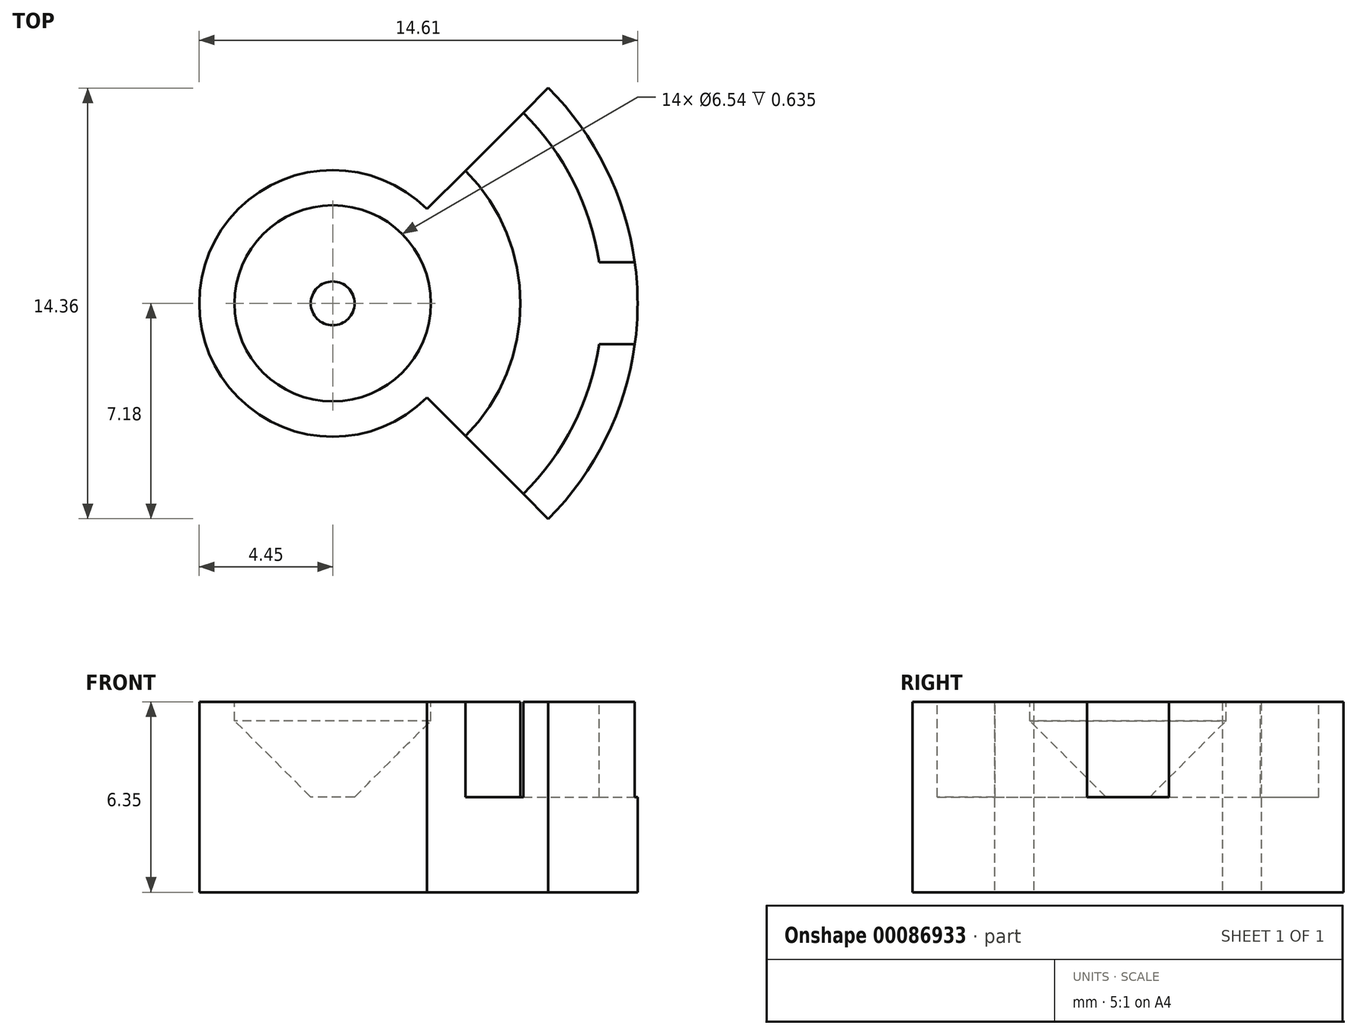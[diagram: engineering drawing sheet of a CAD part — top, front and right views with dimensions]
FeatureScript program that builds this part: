
annotation { "Feature Type Name" : "Feature", "Feature Type Description" : "" }
export const myFeature = defineFeature(function(context is Context, id is Id, definition is map)
    precondition{}
    {
        {
            var Q0;
            Q0=qCreatedBy(makeId("Top.planeOp"),FACE);
            var sketch = newSketch(context, id + "F0", { "sketchPlane" : qUnion([Q0])});
            skCircle(sketch, "E0", {"center": v(0, 0) * mm, "radius": 3.27 * mm});
            skCircle(sketch, "E1", {"center": v(0, 0) * mm, "radius": 4.45 * mm});
            skLineSegment(sketch, "E2", {"start": v(0, 11.64) * mm, "end": v(0, -10.82) * mm, "construction": true});
            skArc(sketch, "E3", {"start": v(-4.45, 0) * mm, "mid": v(-4.1, 1.7) * mm, "end": v(-3.14, 3.14) * mm});
            skLineSegment(sketch, "E4", {"start": v(0, 0) * mm, "end": v(-7.18, 7.18) * mm, "construction": true});
            skArc(sketch, "E5", {"start": v(-10.16, 0) * mm, "mid": v(-9.39, 3.89) * mm, "end": v(-7.18, 7.18) * mm});
            skLineSegment(sketch, "E6", {"start": v(-21.14, 0) * mm, "end": v(20.83, 0) * mm, "construction": true});
            skLineSegment(sketch, "E7", {"start": v(-3.14, 3.14) * mm, "end": v(-7.18, 7.18) * mm});
            skArc(sketch, "E8.MirrorCS", {"start": v(4.45, 0) * mm, "mid": v(4.1, 1.7) * mm, "end": v(3.14, 3.14) * mm});
            skLineSegment(sketch, "E9.MirrorCS", {"start": v(3.14, 3.14) * mm, "end": v(7.18, 7.18) * mm});
            skArc(sketch, "E10.MirrorCS", {"start": v(10.16, 0) * mm, "mid": v(9.39, 3.89) * mm, "end": v(7.18, 7.18) * mm});
            skArc(sketch, "E11.MirrorCS", {"start": v(-10.16, 0) * mm, "mid": v(-9.39, -3.89) * mm, "end": v(-7.18, -7.18) * mm});
            skLineSegment(sketch, "E12.MirrorCS", {"start": v(-3.14, -3.14) * mm, "end": v(-7.18, -7.18) * mm});
            skArc(sketch, "E13.MirrorCS", {"start": v(-4.45, 0) * mm, "mid": v(-4.1, -1.7) * mm, "end": v(-3.14, -3.14) * mm});
            skArc(sketch, "E14.MirrorCS", {"start": v(4.45, 0) * mm, "mid": v(4.1, -1.7) * mm, "end": v(3.14, -3.14) * mm});
            skLineSegment(sketch, "E15.MirrorCS", {"start": v(3.14, -3.14) * mm, "end": v(7.18, -7.18) * mm});
            skArc(sketch, "E16.MirrorCS", {"start": v(10.16, 0) * mm, "mid": v(9.39, -3.89) * mm, "end": v(7.18, -7.18) * mm});
            skSolve(sketch);
        }
        {
            var Q0;
            Q0=makeQuery(id+"F0.imprint","IMPRINT",FACE,{"disambiguationData":[TD([[makeQuery(id+"F0.imprint","IMPRINT",EDGE,{"derivedFrom":sQuery(id+"F0.wireOp",EDGE,"E5")}),-1.0]])]});
            var Q1;
            {var subQ1=sQuery(id+"F0.wireOp",EDGE,"gBuVnUFR-Onij-r1q8-XpBl-5uBVs7pSRJUX");Q1=makeQuery(id+"F0.imprint","IMPRINT",FACE,{"disambiguationData":[TD([[makeQuery(id+"F0.imprint","IMPRINT",EDGE,{"derivedFrom":subQ1}),1.0]])]});}
            var Q2;
            Q2=makeQuery(id+"F0.imprint","IMPRINT",FACE,{"disambiguationData":[TD([[makeQuery(id+"F0.imprint","IMPRINT",EDGE,{"derivedFrom":sQuery(id+"F0.wireOp",EDGE,"E0")}),-1.0]])]});
            var Q3;
            {var subQ1=sQuery(id+"F0.wireOp",EDGE,"1faedc89-acef-45de-ba8b-80695d0e1f000.MirrorCS");Q3=makeQuery(id+"F0.imprint","IMPRINT",FACE,{"disambiguationData":[TD([[makeQuery(id+"F0.imprint","IMPRINT",EDGE,{"derivedFrom":subQ1}),-1.0]])]});}
            var Q4;
            {var subQ0=sQuery(id+"F0.wireOp",EDGE,"E9.MirrorCS");Q4=makeQuery(id+"F0.imprint","IMPRINT",FACE,{"disambiguationData":[TD([[makeQuery(id+"F0.imprint","IMPRINT",EDGE,{"derivedFrom":subQ0}),-1.0]])]});}
            var Q5;
            Q5=makeQuery(id+"F0.imprint","IMPRINT",FACE,{"disambiguationData":[TD([[makeQuery(id+"F0.imprint","IMPRINT",EDGE,{"derivedFrom":sQuery(id+"F0.wireOp",EDGE,"E0")}),1.0]])]});
            extrude(context, id + "F1", {"entities" : qUnion([Q0, Q1, Q2, Q3, Q4, Q5]), "depth" : 6.35 * mm});
        }
        {
            var Q0;
            Q0=makeQuery(id+"F1.opExtrude","CAP_FACE",FACE,{"disambiguationData":[OSD([sQuery(id+"F0.wireOp",EDGE,"E0"),sQuery(id+"F0.wireOp",EDGE,"E1"),sQuery(id+"F0.wireOp",EDGE,"gBuVnUFR-Onij-r1q8-XpBl-5uBVs7pSRJUX"),sQuery(id+"F0.wireOp",EDGE,"E3"),sQuery(id+"F0.wireOp",EDGE,"E5"),sQuery(id+"F0.wireOp",EDGE,"E7"),sQuery(id+"F0.wireOp",EDGE,"1faedc89-acef-45de-ba8b-80695d0e1f000.MirrorCS"),sQuery(id+"F0.wireOp",EDGE,"E8.MirrorCS"),sQuery(id+"F0.wireOp",EDGE,"E9.MirrorCS"),sQuery(id+"F0.wireOp",EDGE,"E10.MirrorCS"),sQuery(id+"F0.wireOp",EDGE,"E11.MirrorCS"),sQuery(id+"F0.wireOp",EDGE,"E12.MirrorCS"),sQuery(id+"F0.wireOp",EDGE,"E13.MirrorCS"),sQuery(id+"F0.wireOp",EDGE,"ab77834b-439c-4acf-8903-ebee9be9d7cb0.MirrorCS"),sQuery(id+"F0.wireOp",EDGE,"17798d41-e0fd-403b-97c7-1fccfac1d1220.MirrorCS"),sQuery(id+"F0.wireOp",EDGE,"E14.MirrorCS"),sQuery(id+"F0.wireOp",EDGE,"E15.MirrorCS"),sQuery(id+"F0.wireOp",EDGE,"E16.MirrorCS")])],"isStart":false});
            var sketch = newSketch(context, id + "F2", { "sketchPlane" : qUnion([Q0])});
            skCircle(sketch, "E17", {"center": v(0, 0) * mm, "radius": 6.25 * mm});
            skCircle(sketch, "E18", {"center": v(0, 0) * mm, "radius": 8.99 * mm});
            skLineSegment(sketch, "E19", {"start": v(-8.88, 1.37) * mm, "end": v(-10.07, 1.37) * mm});
            skLineSegment(sketch, "E20", {"start": v(-10.16, 0) * mm, "end": v(10.16, 0) * mm, "construction": true});
            skLineSegment(sketch, "E21", {"start": v(0, 8.99) * mm, "end": v(0, -8.99) * mm, "construction": true});
            skLineSegment(sketch, "E22.MirrorCS", {"start": v(-8.88, -1.37) * mm, "end": v(-10.07, -1.37) * mm});
            skLineSegment(sketch, "E23.MirrorCS", {"start": v(8.88, 1.37) * mm, "end": v(10.07, 1.37) * mm});
            skLineSegment(sketch, "E24.MirrorCS", {"start": v(8.88, -1.37) * mm, "end": v(10.07, -1.37) * mm});
            skCircle(sketch, "E25", {"center": v(0, 0) * mm, "radius": 3.27 * mm});
            skSolve(sketch);
        }
        {
            var Q0;
            {var subQ3=makeQuery(id+"F1.opExtrude","CAP_EDGE",EDGE,{"disambiguationData":[OSD([sQuery(id+"F0.wireOp",EDGE,"E7")])],"isStart":false});var subQ7=sQuery(id+"F2.wireOp",EDGE,"E17");var subQ9=makeQuery(id+"F2.imprint","INTERSECT",VERTEX,{"derivedFrom":[subQ3,subQ7]});Q0=makeQuery(id+"F2.imprint","IMPRINT",FACE,{"disambiguationData":[TD([[makeQuery(id+"F2.imprint","IMPRINT",EDGE,{"disambiguationData":[TD([[subQ9,-1.0]])],"derivedFrom":subQ7}),-1.0]])]});}
            var Q1;
            {var subQ2=makeQuery(id+"F1.opExtrude","CAP_EDGE",EDGE,{"disambiguationData":[OSD([sQuery(id+"F0.wireOp",EDGE,"E9.MirrorCS")])],"isStart":false});var subQ7=sQuery(id+"F2.wireOp",EDGE,"E17");var subQ8=makeQuery(id+"F2.imprint","INTERSECT",VERTEX,{"derivedFrom":[subQ2,subQ7]});Q1=makeQuery(id+"F2.imprint","IMPRINT",FACE,{"disambiguationData":[TD([[makeQuery(id+"F2.imprint","IMPRINT",EDGE,{"disambiguationData":[TD([[subQ8,1.0]])],"derivedFrom":subQ7}),-1.0]])]});}
            var Q2;
            {var subQ0=sQuery(id+"F2.wireOp",EDGE,"E19");Q2=makeQuery(id+"F2.imprint","IMPRINT",FACE,{"disambiguationData":[TD([[makeQuery(id+"F2.imprint","IMPRINT",EDGE,{"derivedFrom":subQ0}),1.0]])]});}
            var Q3;
            {var subQ0=sQuery(id+"F2.wireOp",EDGE,"E23.MirrorCS");Q3=makeQuery(id+"F2.imprint","IMPRINT",FACE,{"disambiguationData":[TD([[makeQuery(id+"F2.imprint","IMPRINT",EDGE,{"derivedFrom":subQ0}),-1.0]])]});}
            var Q4;
            Q4=makeQuery(id+"F2.imprint","IMPRINT",FACE,{"disambiguationData":[TD([[makeQuery(id+"F2.imprint","IMPRINT",EDGE,{"derivedFrom":sQuery(id+"F2.wireOp",EDGE,"E25")}),1.0]])]});
            extrude(context, id + "F3", {"entities" : qUnion([Q0, Q1, Q2, Q3, Q4]), "operationType" : NewBodyOperationType.REMOVE, "oppositeDirection" : true, "depth" : 3.17 * mm});
        }
        {
            var Q0;
            Q0=makeQuery(id+"F3.boolean.opBoolean","COPY",EDGE,{"derivedFrom":makeQuery(id+"F3.opExtrude","CAP_EDGE",EDGE,{"disambiguationData":[OSD([sQuery(id+"F2.wireOp",EDGE,"E25")])],"isStart":false})});
            chamfer(context, id + "F4", {"entities" : qUnion([Q0]), "width" : 2.54 * mm, "tangentPropagation" : true});
        }
    });
